# Revit family: PlumFix_Tap_ABEY_Park Avenue_High Basin Mixer
name_source: partatom
category: Plumbing Fixtures
revit_build: Autodesk Revit 2015 (Build: 20140223_1515(x64)
units: mm (PartAtom-declared; Revit-internal decimal feet)

## types (3) — shared parameters
CW Connection = Yes
Description = High Basin Mixer
HW Connection = Yes
Manufacturer = Abey Australia
Manufacturer_Overall Depth = 235 mm
Manufacturer_Overall Height = 302 mm  [stored 0.990814 ft]
Manufacturer_Overall Width = 50 mm  [stored 0.164042 ft]
Manufacturer_URL__Product Specific = https://www.abey.com.au
URL = https://www.abey.com.au
Vent Connection = No
Waste Connection = No
zero-valued in all types: CWFU, Cost, HWFU, WFU

## per-type parameters (varying)
| type | Manufacturer_Spec Code | Model | PlumbingMaterial_ANZRS | Type Comments |
| Chrome | 1B2 | 1B2 | z_Abey_Chrome | Chrome Finish |
| Black | 1B2-B | 1B2-B | z_Abey_Black | Black Finish |
| Gun Metal | 1B2-GM | 1B2-GM | z_Abey_Gun Metal | Gun Metal Finish |

note: [stored X ft] marks values corroborated as IEEE doubles in the binary element streams (Revit-internal decimal feet)

## geometry (parser evidence)
native form markers: Sweep x2
no freeform markers — native parametric forms only
